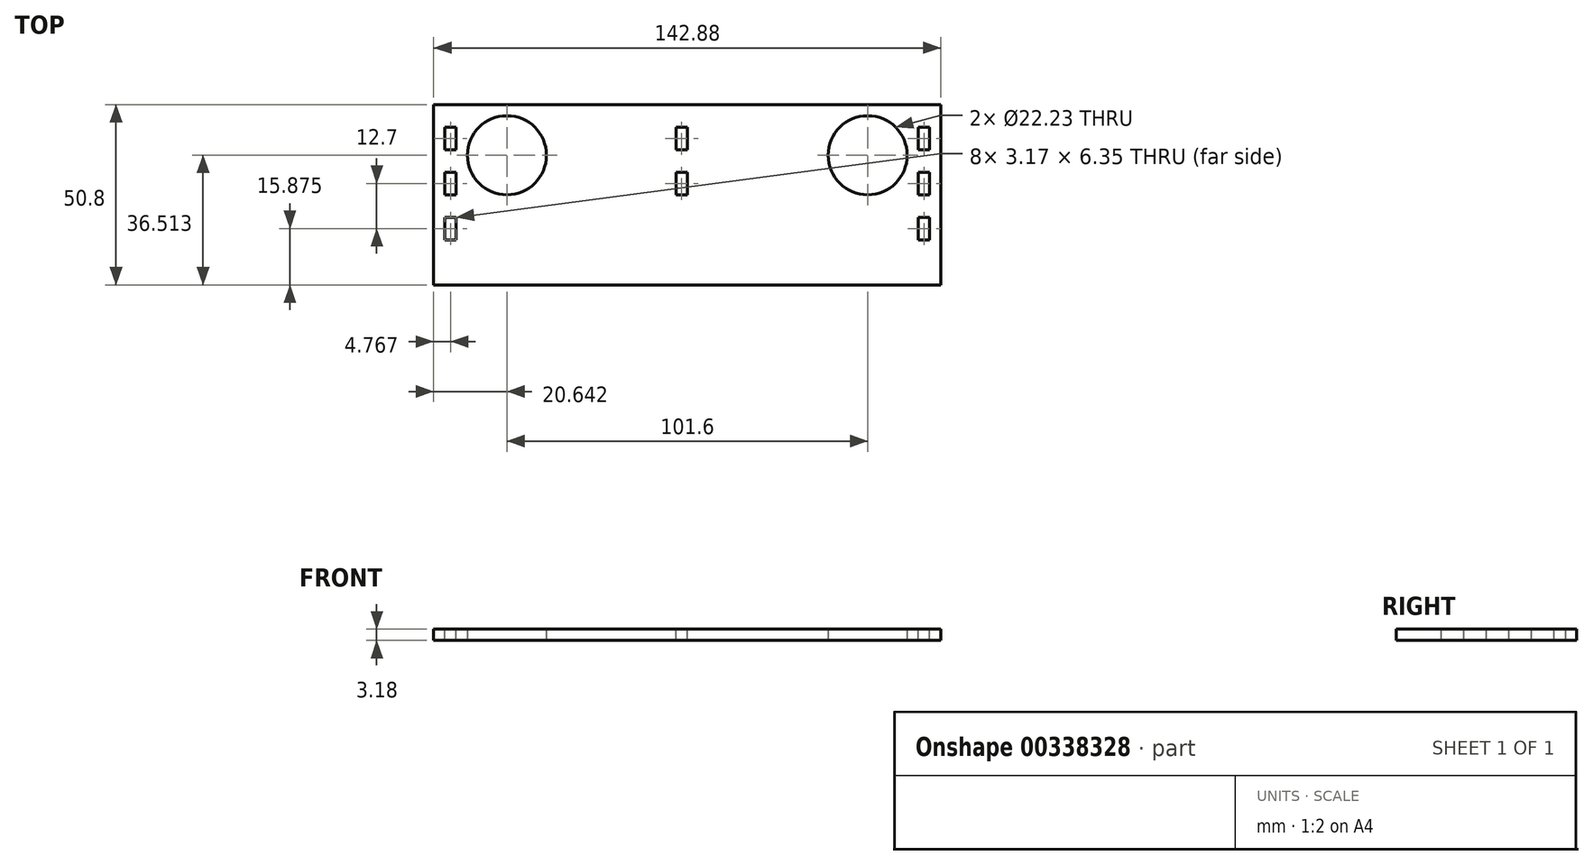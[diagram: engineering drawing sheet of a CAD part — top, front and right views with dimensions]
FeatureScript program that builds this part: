
annotation { "Feature Type Name" : "Feature", "Feature Type Description" : "" }
export const myFeature = defineFeature(function(context is Context, id is Id, definition is map)
    precondition{}
    {
        {
            var Q0;
            Q0=qCreatedBy(makeId("Top.planeOp"),FACE);
            var sketch = newSketch(context, id + "F0", { "sketchPlane" : qUnion([Q0])});
            skLineSegment(sketch, "E0.bottom", {"start": v(0, 0) * mm, "end": v(-142.87, 0) * mm});
            skLineSegment(sketch, "E0.top", {"start": v(0, 50.8) * mm, "end": v(-142.88, 50.8) * mm});
            skLineSegment(sketch, "E0.left", {"start": v(0, 0) * mm, "end": v(0, 50.8) * mm});
            skLineSegment(sketch, "E0.right", {"start": v(-142.88, 0) * mm, "end": v(-142.88, 50.8) * mm});
            skLineSegment(sketch, "E1", {"start": v(-71.44, 50.8) * mm, "end": v(-71.44, 36.51) * mm, "construction": true});
            skLineSegment(sketch, "E2", {"start": v(-122.24, 36.51) * mm, "end": v(-20.64, 36.51) * mm, "construction": true});
            skCircle(sketch, "E3", {"center": v(-122.24, 36.51) * mm, "radius": 11.11 * mm});
            skCircle(sketch, "E4", {"center": v(-20.64, 36.51) * mm, "radius": 11.11 * mm});
            skLineSegment(sketch, "E5", {"start": v(-20.64, 36.51) * mm, "end": v(-9.52, 36.51) * mm, "construction": true});
            skLineSegment(sketch, "E6", {"start": v(-9.52, 36.51) * mm, "end": v(0, 36.51) * mm, "construction": true});
            skSolve(sketch);
        }
        {
            var Q0;
            Q0 = qSketchRegion(id + "F0", true);
            extrude(context, id + "F1", {"entities" : qUnion([Q0]), "depth" : 3.17 * mm});
        }
        {
            var Q0;
            Q0=makeQuery(id+"F1.opExtrude","CAP_FACE",FACE,{"disambiguationData":[OSD([sQuery(id+"F0.wireOp",EDGE,"E0.bottom"),sQuery(id+"F0.wireOp",EDGE,"E0.top"),sQuery(id+"F0.wireOp",EDGE,"E0.left"),sQuery(id+"F0.wireOp",EDGE,"E0.right"),sQuery(id+"F0.wireOp",EDGE,"E3"),sQuery(id+"F0.wireOp",EDGE,"E4")])],"isStart":false});
            var sketch = newSketch(context, id + "F2", { "sketchPlane" : qUnion([Q0])});
            skLineSegment(sketch, "E7.bottom", {"start": v(-6.35, 44.45) * mm, "end": v(-3.17, 44.45) * mm});
            skLineSegment(sketch, "E7.top", {"start": v(-6.35, 38.1) * mm, "end": v(-3.17, 38.1) * mm});
            skLineSegment(sketch, "E7.left", {"start": v(-6.35, 44.45) * mm, "end": v(-6.35, 38.1) * mm});
            skLineSegment(sketch, "E7.right", {"start": v(-3.17, 44.45) * mm, "end": v(-3.17, 38.1) * mm});
            skLineSegment(sketch, "E8.bottom", {"start": v(-6.35, 31.75) * mm, "end": v(-3.17, 31.75) * mm});
            skLineSegment(sketch, "E8.top", {"start": v(-6.35, 25.4) * mm, "end": v(-3.17, 25.4) * mm});
            skLineSegment(sketch, "E8.left", {"start": v(-6.35, 31.75) * mm, "end": v(-6.35, 25.4) * mm});
            skLineSegment(sketch, "E8.right", {"start": v(-3.17, 31.75) * mm, "end": v(-3.17, 25.4) * mm});
            skLineSegment(sketch, "E9.bottom", {"start": v(-6.35, 19.05) * mm, "end": v(-3.17, 19.05) * mm});
            skLineSegment(sketch, "E9.top", {"start": v(-6.35, 12.7) * mm, "end": v(-3.17, 12.7) * mm});
            skLineSegment(sketch, "E9.left", {"start": v(-6.35, 19.05) * mm, "end": v(-6.35, 12.7) * mm});
            skLineSegment(sketch, "E9.right", {"start": v(-3.17, 19.05) * mm, "end": v(-3.17, 12.7) * mm});
            skLineSegment(sketch, "E10", {"start": v(-4.76, 44.45) * mm, "end": v(-4.76, 50.8) * mm, "construction": true});
            skLineSegment(sketch, "E11", {"start": v(-4.76, 38.1) * mm, "end": v(-4.76, 31.75) * mm, "construction": true});
            skLineSegment(sketch, "E12", {"start": v(-4.76, 25.4) * mm, "end": v(-4.76, 19.05) * mm, "construction": true});
            skLineSegment(sketch, "E13", {"start": v(-4.76, 12.7) * mm, "end": v(-4.76, 6.35) * mm, "construction": true});
            skLineSegment(sketch, "E14", {"start": v(-3.17, 44.45) * mm, "end": v(0, 44.45) * mm, "construction": true});
            skLineSegment(sketch, "E15.bottom", {"start": v(-139.7, 44.45) * mm, "end": v(-136.53, 44.45) * mm});
            skLineSegment(sketch, "E15.top", {"start": v(-139.7, 38.1) * mm, "end": v(-136.53, 38.1) * mm});
            skLineSegment(sketch, "E15.left", {"start": v(-139.7, 44.45) * mm, "end": v(-139.7, 38.1) * mm});
            skLineSegment(sketch, "E15.right", {"start": v(-136.53, 44.45) * mm, "end": v(-136.53, 38.1) * mm});
            skLineSegment(sketch, "E16.bottom", {"start": v(-139.7, 31.75) * mm, "end": v(-136.53, 31.75) * mm});
            skLineSegment(sketch, "E16.top", {"start": v(-139.7, 25.4) * mm, "end": v(-136.53, 25.4) * mm});
            skLineSegment(sketch, "E16.left", {"start": v(-139.7, 31.75) * mm, "end": v(-139.7, 25.4) * mm});
            skLineSegment(sketch, "E16.right", {"start": v(-136.53, 31.75) * mm, "end": v(-136.53, 25.4) * mm});
            skLineSegment(sketch, "E17.bottom", {"start": v(-139.7, 19.05) * mm, "end": v(-136.53, 19.05) * mm});
            skLineSegment(sketch, "E17.top", {"start": v(-139.7, 12.7) * mm, "end": v(-136.53, 12.7) * mm});
            skLineSegment(sketch, "E17.left", {"start": v(-139.7, 19.05) * mm, "end": v(-139.7, 12.7) * mm});
            skLineSegment(sketch, "E17.right", {"start": v(-136.53, 19.05) * mm, "end": v(-136.53, 12.7) * mm});
            skLineSegment(sketch, "E18.bottom", {"start": v(-74.61, 44.45) * mm, "end": v(-71.44, 44.45) * mm});
            skLineSegment(sketch, "E18.top", {"start": v(-74.61, 38.1) * mm, "end": v(-71.44, 38.1) * mm});
            skLineSegment(sketch, "E18.left", {"start": v(-74.61, 44.45) * mm, "end": v(-74.61, 38.1) * mm});
            skLineSegment(sketch, "E18.right", {"start": v(-71.44, 44.45) * mm, "end": v(-71.44, 38.1) * mm});
            skLineSegment(sketch, "E19.bottom", {"start": v(-74.61, 31.75) * mm, "end": v(-71.44, 31.75) * mm});
            skLineSegment(sketch, "E19.top", {"start": v(-74.61, 25.4) * mm, "end": v(-71.44, 25.4) * mm});
            skLineSegment(sketch, "E19.left", {"start": v(-74.61, 31.75) * mm, "end": v(-74.61, 25.4) * mm});
            skLineSegment(sketch, "E19.right", {"start": v(-71.44, 31.75) * mm, "end": v(-71.44, 25.4) * mm});
            skLineSegment(sketch, "E20", {"start": v(-139.7, 44.45) * mm, "end": v(-139.7, 50.8) * mm, "construction": true});
            skLineSegment(sketch, "E21", {"start": v(-139.7, 44.45) * mm, "end": v(-142.88, 44.45) * mm, "construction": true});
            skLineSegment(sketch, "E22", {"start": v(-139.7, 38.1) * mm, "end": v(-139.7, 31.75) * mm, "construction": true});
            skLineSegment(sketch, "E23", {"start": v(-139.7, 25.4) * mm, "end": v(-139.7, 19.05) * mm, "construction": true});
            skLineSegment(sketch, "E24", {"start": v(-20.64, 36.51) * mm, "end": v(-71.44, 36.51) * mm, "construction": true});
            skLineSegment(sketch, "E25", {"start": v(-71.44, 44.45) * mm, "end": v(-71.44, 50.8) * mm, "construction": true});
            skLineSegment(sketch, "E26", {"start": v(-71.44, 38.1) * mm, "end": v(-71.44, 31.75) * mm, "construction": true});
            skSolve(sketch);
        }
        {
            var Q0;
            Q0 = qSketchRegion(id + "F2", true);
            var Q1;
            Q1=makeQuery(id+"F1.opExtrude","CAP_FACE",FACE,{"disambiguationData":[OSD([sQuery(id+"F0.wireOp",EDGE,"E0.bottom"),sQuery(id+"F0.wireOp",EDGE,"E0.top"),sQuery(id+"F0.wireOp",EDGE,"E0.left"),sQuery(id+"F0.wireOp",EDGE,"E0.right"),sQuery(id+"F0.wireOp",EDGE,"E3"),sQuery(id+"F0.wireOp",EDGE,"E4")])],"isStart":true});
            extrude(context, id + "F3", {"entities" : qUnion([Q0]), "operationType" : NewBodyOperationType.REMOVE, "endBound" : BoundingType.UP_TO_SURFACE, "oppositeDirection" : true, "endBoundEntityFace" : qUnion([Q1]), "depth" : 25.4 * mm});
        }
    });
